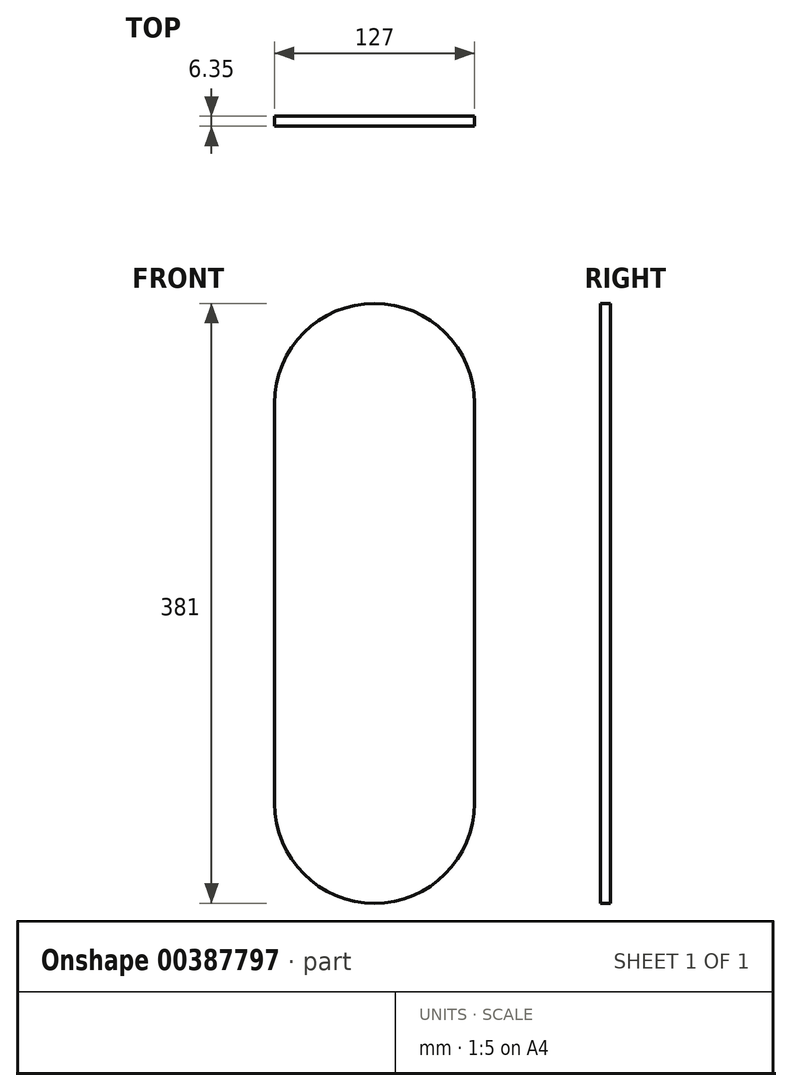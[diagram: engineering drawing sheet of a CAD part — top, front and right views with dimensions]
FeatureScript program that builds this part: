
annotation { "Feature Type Name" : "Feature", "Feature Type Description" : "" }
export const myFeature = defineFeature(function(context is Context, id is Id, definition is map)
    precondition{}
    {
        {
            var Q0;
            Q0=qCreatedBy(makeId("Front.planeOp"),FACE);
            var sketch = newSketch(context, id + "F0", { "sketchPlane" : qUnion([Q0])});
            skLineSegment(sketch, "E0.bottom", {"start": v(-63.5, -127) * mm, "end": v(63.5, -127) * mm});
            skLineSegment(sketch, "E0.top", {"start": v(-63.5, 127) * mm, "end": v(63.5, 127) * mm});
            skLineSegment(sketch, "E0.left", {"start": v(-63.5, -127) * mm, "end": v(-63.5, 127) * mm});
            skLineSegment(sketch, "E0.right", {"start": v(63.5, -127) * mm, "end": v(63.5, 127) * mm});
            skArc(sketch, "E1", {"start": v(63.5, 127) * mm, "mid": v(0, 190.5) * mm, "end": v(-63.5, 127) * mm});
            skArc(sketch, "E2", {"start": v(-63.5, -127) * mm, "mid": v(0, -190.5) * mm, "end": v(63.5, -127) * mm});
            skSolve(sketch);
        }
        {
            var Q0;
            Q0=makeQuery(id+"F0.imprint","IMPRINT",FACE,{"disambiguationData":[TD([[makeQuery(id+"F0.imprint","IMPRINT",EDGE,{"derivedFrom":sQuery(id+"F0.wireOp",EDGE,"E0.top")}),1.0]])]});
            var Q1;
            Q1=makeQuery(id+"F0.imprint","IMPRINT",FACE,{"disambiguationData":[TD([[makeQuery(id+"F0.imprint","IMPRINT",EDGE,{"derivedFrom":sQuery(id+"F0.wireOp",EDGE,"E0.bottom")}),1.0]])]});
            var Q2;
            Q2=makeQuery(id+"F0.imprint","IMPRINT",FACE,{"disambiguationData":[TD([[makeQuery(id+"F0.imprint","IMPRINT",EDGE,{"derivedFrom":sQuery(id+"F0.wireOp",EDGE,"E0.bottom")}),-1.0]])]});
            extrude(context, id + "F1", {"entities" : qUnion([Q0, Q1, Q2]), "depth" : 6.35 * mm});
        }
    });
